# Revit family: 6294_Klemmset G1_2 (metallisch dichtend)
name_source: partatom
category: Rohrformteile
units: mm (PartAtom-declared; Revit-internal decimal feet)

## family parameters
Arbeitsebenenbasiert = Nein
Beim Laden mit Abzugskörper schneiden = Nein
Bemaßung runder Anschluss = Durchmesser verwenden
Gemeinsam genutzt = Nein
Immer vertikal = Ja
OmniClass-Nummer = 23.65.55.14
OmniClass-Titel = Valves for Liquid Services
Teiletyp = Verbindung

## types (1)
- G1/2 x 15x1
    Anwendungsgebiet = Der Klemmring stellt eine absolut sichere Verbindung zwischen dem Ventilgehäuse und dem Rohr dar.
Diese Verbindung eignet sich besonders für Kupferrohre und dünnwandige Stahlrohre und kann bei Bedarf jederzeit gelöst werden.
Eine einwandfreie Dichtheit auf Dauer ist dann gegeben, wenn die Montage gemäß der Verarbeitungsanleitung durchgeführt wurde.


Nach Anzug der Klemmschraube verkeilt sich der Klemmring zwischen Rohrwand und Innenkonus von Gehäuse und Klemmschraube.
Dabei wird das Rohr in seiner Lage durch Kraftschluss fixiert und gegen Axialverschiebung gesichert.
Die dabei entstehende Pressung sorgt für sichere Dichtheit.
Die innen im Klemmring befindlichen Rillen stellen eine Labyrinthdichtung dar und helfen Unebenheiten des Rohres zu überbrücken.

Die Klemmverschraubung kann mehrmals gelöst werden und stellt eine einfache und sichere Verbindung dar.
Für die Güte der Verbindung ist es wichtig, dass das Rohr gegen den Anschlag im Innenkonus stößt, also ausreichend tief eingeschoben ist.

Die asymetrischen Klemmringe (6274, 6284, 6294) mit integrierten Reduzierhüllen ermöglichen den Rohranschluss von Rohren mit Durchmesser 8 - 16mm an einen Ventilkörper.
Diese Ausführung stellt ein Optimum an Kombinationsmöglichkeiten sicher.
    Ausführung = 6294 G1/2 - 15mm:
Klemmring metallisch dichtend zum Rohr, Klemmringmutter G 1/2.
Einsetzbar für Weichstahl- und Kupferrohre.
Nicht geeignet für verchromte Metallrohre oder Edelstahlrohre.
    Hersteller = HERZ Armaturen Ges.m.b.H.
    KH01 = 1.1 mm
    KL01 = 3 mm  [stored 0.00984252 ft]
    Klemmring = CW614N
    ML03 = 10.8 mm  [stored 0.0354331 ft]
    Max. Betriebsdruck = gemäß EN 1254-2: 1988, Tabelle 5
    Max. Betriebstemperatur = 110 °C
    Medium = Heizungswasser nach ÖNORM H5195 oder VDI- Richtlinie 2035.
Die Verwendung von Ethylen- oder Propyleneglykol in einem Mischungsverhältnis 25- 50% ist zulässig.
    Mutter = CW614N, G 1/2
    S01 = 5 mm  [stored 0.0164042 ft]
    S02 = 5 mm  [stored 0.0164042 ft]
    SCRNCODE = 07;01;02
    SCRNSEQ = AWI;AWI_TYP="1001";2
    URL = www.herz-armaturen.at
    Vorgabe-Ansicht = 0 mm  [stored 0 ft]

note: [stored X ft] marks values corroborated as IEEE doubles in the binary element streams (Revit-internal decimal feet)
